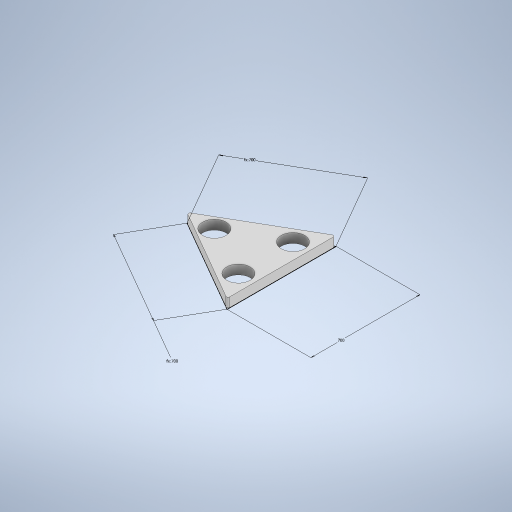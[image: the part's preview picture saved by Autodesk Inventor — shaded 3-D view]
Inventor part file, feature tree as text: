
AUTODESK INVENTOR PART (.ipt)
format: ipt  version: 2023.2 (Build 272271000, 271)  size: 267,264 bytes
history: native  units: mm
features: fillet x3, sketch x1, extrude x1, hole x1
ambient origin geometry x8: Origin, YZ Plane, XZ Plane, XY Plane, X Axis, Y Axis, Z Axis, Center Point
bodies: Solid1 (feature_tree)
feature tree (6):
  sketch  "Sketch1"  dims[d0=700.0mm d1=700.0mm d2=700.0mm d3=60.0mm d4=0.0mm d19=150.0mm d20=6.0mm d21=4.0mm d22=2.0mm d23=90.0deg d24=8.0mm d25=20.594885mm d26=10.0mm d27=10.0mm d28=10.0mm d5=1.0mm d6=1.0mm d7=1.0mm d8=0.15mm d9=0.25mm d10=0.375mm d11=14.3117mm d12=0.75mm d13=20.594885mm d14=0.0625mm d15=0.75mm d16=0.375mm]
  extrude  "Extrusion1"  Depth=700.0mm
  hole  "Hole3"  [1 undecoded]
  fillet  "Fillet1"  Radius=60.0mm
  fillet  "Fillet2"  Radius=10.0mm
  fillet  "Fillet3"  Radius=10.0mm
note: 1 required parameter value undecoded (feature->parameter linkage not recoverable at this tier; creation-order binding heuristic only, values carry confidence <= 0.55)
